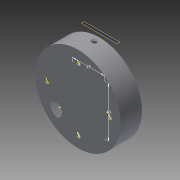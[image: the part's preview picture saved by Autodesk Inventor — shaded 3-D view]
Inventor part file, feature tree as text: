
AUTODESK INVENTOR PART (.ipt)
format: ipt  version: 2014 (Build 180170000, 170)  size: 240,640 bytes
history: native  units: mm
features: sketch x10, extrude x8, chamfer x5, projected_geometry x3, reference x2, plane x1
ambient origin geometry x8: Origin, YZ Plane, XZ Plane, XY Plane, X Axis, Y Axis, Z Axis, Center Point
bodies: Solid1 (feature_tree)
feature tree (29):
  extrude  "Extrusion1"  Depth=3.0mm TaperAngle=0.0deg
  extrude  "Extrusion2"  Depth=14.0mm TaperAngle=0.0deg
  extrude  "Extrusion3"  Depth=4.0mm
  chamfer  "Chamfer1"  Distance=14.0mm
  extrude  "Extrusion4"  Depth=10.0mm
  chamfer  "Chamfer2"  Distance=14.0mm
  sketch  "Sketch5"  dims[d9=4.0mm]
  extrude  "Extrusion5"  Depth=6.0mm TaperAngle=45.0deg
  extrude  "Extrusion6"  Depth=6.0mm
  chamfer  "Chamfer3"  Distance=40.0mm
  sketch  "Sketch8"  dims[d12=25.0mm]
  plane  "Work Plane1"
  extrude  "Extrusion9"  Depth=6.0mm
  chamfer  "Chamfer5"  Distance=6.0mm
  extrude  "Extrusion10"  Depth=6.0mm
  chamfer  "Chamfer6"  Distance=6.0mm
  sketch  "Sketch1"  dims[d0=68.0mm d1=3.0mm d2=0.0mm]
  sketch  "Sketch2"  dims[d3=62.0mm d4=14.0mm d5=0.0mm]
  sketch  "Sketch3"  dims[d6=4.0mm d7=4.0mm]
  sketch  "Sketch4"  dims[d8=4.0mm]
  sketch  "Sketch6"  dims[d10=25.0mm]
  sketch  "Sketch7"  dims[d11=25.0mm]
  projected_geometry  "Projected Loop1"
  projected_geometry  "Projected Loop2"
  projected_geometry  "Projected Loop3"
  reference  "Reference1"
  reference  "Reference2"
  sketch  "Sketch10"  dims[d13=25.0mm d14=14.0mm d15=0.0mm]
  sketch  "Sketch11"  dims[d16=2.0mm d17=2.0mm d18=45.0deg d19=10.0mm d20=14.0mm d21=0.0mm d22=3.0mm d23=2.0mm d24=45.0deg d25=25.0mm d26=40.0mm d27=2.5mm d28=6.0mm d29=2.5mm d30=6.0mm d31=2.5mm d32=6.0mm d33=2.5mm d34=6.0mm d35=25.0mm d36=40.0mm d37=3.0mm d38=3.0mm d39=3.0mm d40=3.0mm d41=3.0mm d42=3.0mm d43=3.0mm d44=3.0mm d45=3.0mm d46=0.0mm d47=2.0mm d48=0.0mm d49=0.6mm d50=2.0mm d51=45.0deg d62=6.0mm d63=0.0mm d64=4.0mm d65=2.0mm d66=45.0deg d67=59.0mm d68=2.0mm d69=2.0mm d70=6.0mm d71=0.0mm d72=0.5mm d73=2.0mm d74=45.0deg]
